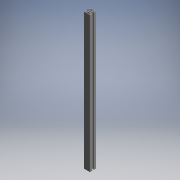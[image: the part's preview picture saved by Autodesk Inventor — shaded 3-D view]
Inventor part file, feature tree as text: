
AUTODESK INVENTOR PART (.ipt)
format: ipt  version: 2017.3 (Build 213256000, 256)  size: 295,424 bytes
history: native  units: mm (DEFAULTED — no unit token found)
features: other x7, sketch x4, revolve x2, extrude x1, hole x1
ambient origin geometry x8: Origin, YZ Plane, XZ Plane, XY Plane, X Axis, Y Axis, Z Axis, Center Point
bodies: Solid1 (feature_tree)
feature tree (15):
  extrude  "Extrusion1"  TaperAngle=360.0deg  [1 undecoded]
  hole  "Hole1"  [1 undecoded]
  revolve  "Revolution1"  [1 undecoded]
  revolve  "Revolution2"  [1 undecoded]
  other  "C1_XY"
  other  "C1_YZ"
  other  "C1_ZX"
  other  "C1_X"
  other  "C1_Y"
  other  "C1_Z"
  other  "C1_Center"
  sketch  "Sketch_76"
  sketch  "Sketch2"  dims[d0=437.0mm d1=0.0mm]
  sketch  "Sketch_50"  dims[d2=4.2mm d3=6.0mm d4=4.0mm d5=2.0mm d6=90.0deg d7=437.0mm d8=0.0mm d9=360.0deg]
  sketch  "Sketch_51"  dims[d10=360.0deg d11=0.0mm]
note: 4 required parameter values undecoded (feature->parameter linkage not recoverable at this tier; creation-order binding heuristic only, values carry confidence <= 0.55)
